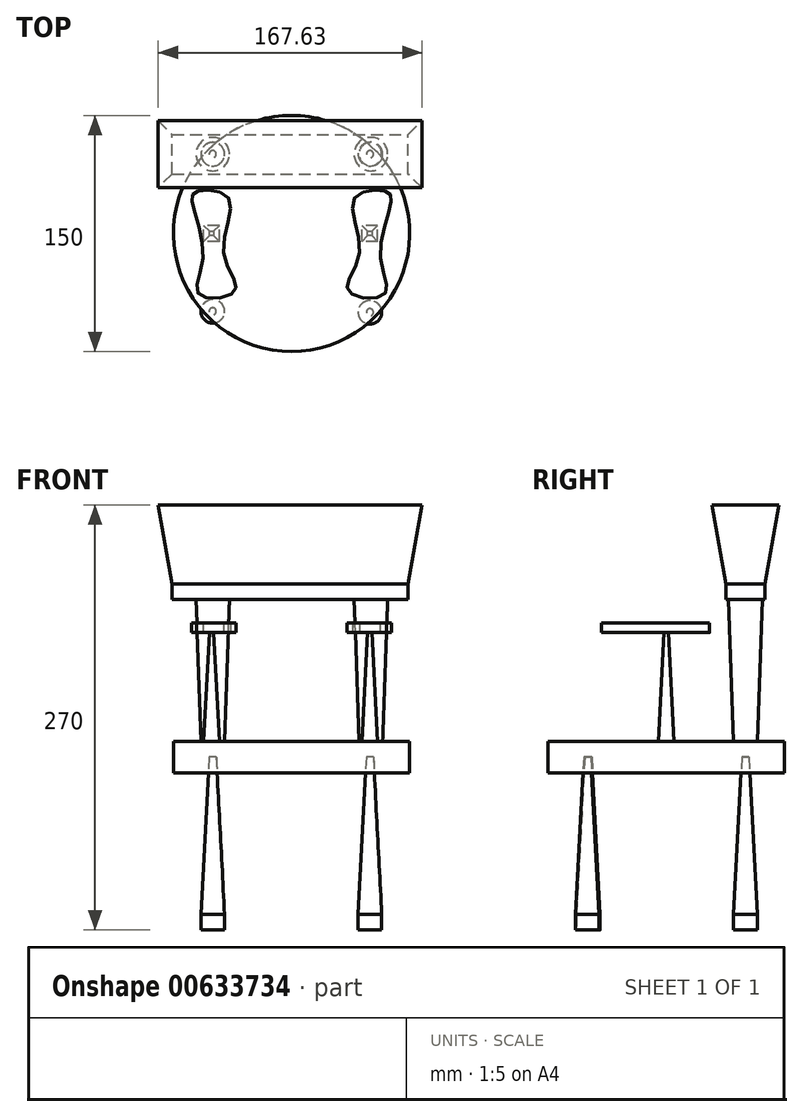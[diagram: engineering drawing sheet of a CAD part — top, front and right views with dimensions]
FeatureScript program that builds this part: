
annotation { "Feature Type Name" : "Feature", "Feature Type Description" : "" }
export const myFeature = defineFeature(function(context is Context, id is Id, definition is map)
    precondition{}
    {
        {
            var Q0;
            Q0=qCreatedBy(makeId("Top.planeOp"),FACE);
            var sketch = newSketch(context, id + "F0", { "sketchPlane" : qUnion([Q0])});
            skCircle(sketch, "E0", {"center": v(-50.07, 50.38) * mm, "radius": 7.5 * mm});
            skCircle(sketch, "E1", {"center": v(49.76, 50.38) * mm, "radius": 7.5 * mm});
            skCircle(sketch, "E2", {"center": v(-50.07, -49.45) * mm, "radius": 7.5 * mm});
            skCircle(sketch, "E3", {"center": v(49.76, -50.07) * mm, "radius": 7.5 * mm});
            skSolve(sketch);
        }
        {
            var Q0;
            Q0=makeQuery(id+"F0.imprint","IMPRINT",FACE,{"disambiguationData":[TD([[makeQuery(id+"F0.imprint","IMPRINT",EDGE,{"derivedFrom":sQuery(id+"F0.wireOp",EDGE,"E1")}),1.0]])]});
            var Q1;
            Q1=makeQuery(id+"F0.imprint","IMPRINT",FACE,{"disambiguationData":[TD([[makeQuery(id+"F0.imprint","IMPRINT",EDGE,{"derivedFrom":sQuery(id+"F0.wireOp",EDGE,"E0")}),1.0]])]});
            var Q2;
            Q2=makeQuery(id+"F0.imprint","IMPRINT",FACE,{"disambiguationData":[TD([[makeQuery(id+"F0.imprint","IMPRINT",EDGE,{"derivedFrom":sQuery(id+"F0.wireOp",EDGE,"E2")}),1.0]])]});
            var Q3;
            Q3=makeQuery(id+"F0.imprint","IMPRINT",FACE,{"disambiguationData":[TD([[makeQuery(id+"F0.imprint","IMPRINT",EDGE,{"derivedFrom":sQuery(id+"F0.wireOp",EDGE,"E3")}),1.0]])]});
            extrude(context, id + "F1", {"entities" : qUnion([Q0, Q1, Q2, Q3]), "depth" : 100 * mm, "offsetDistance" : 25 * mm, "hasDraft" : true, "draftAngle" : 3 * degree, "draftPullDirection" : true, "hasSecondDirection" : true, "secondDirectionOppositeDirection" : true, "secondDirectionDepth" : 10 * mm});
        }
        {
            var Q0;
            Q0=qCreatedBy(makeId("Top.planeOp"),FACE);
            cPlane(context, id + "F2", {"entities" : qUnion([Q0]), "cplaneType" : CPlaneType.OFFSET, "offset" : 100 * mm, "width" : 150 * mm, "height" : 150 * mm});
        }
        {
            var Q0;
            Q0=qCreatedBy(id+"F2.planeOp",FACE);
            var sketch = newSketch(context, id + "F3", { "sketchPlane" : qUnion([Q0])});
            skCircle(sketch, "E4", {"center": v(0, 0) * mm, "radius": 75 * mm});
            skSolve(sketch);
        }
        {
            var Q0;
            Q0=makeQuery(id+"F3.imprint","IMPRINT",FACE,{"disambiguationData":[TD([[makeQuery(id+"F3.imprint","IMPRINT",EDGE,{"derivedFrom":sQuery(id+"F3.wireOp",EDGE,"E4")}),1.0]])]});
            extrude(context, id + "F4", {"entities" : qUnion([Q0]), "depth" : 10 * mm, "offsetDistance" : 25 * mm, "hasSecondDirection" : true, "secondDirectionOppositeDirection" : true, "secondDirectionDepth" : 10 * mm});
        }
        {
            var Q0;
            Q0=qCreatedBy(id+"F2.planeOp",FACE);
            cPlane(context, id + "F5", {"entities" : qUnion([Q0]), "cplaneType" : CPlaneType.OFFSET, "offset" : 10 * mm, "width" : 150 * mm, "height" : 150 * mm});
        }
        {
            var Q0;
            Q0=qCreatedBy(id+"F5.planeOp",FACE);
            var sketch = newSketch(context, id + "F6", { "sketchPlane" : qUnion([Q0])});
            skCircle(sketch, "E5", {"center": v(-50.07, 50.38) * mm, "radius": 7.5 * mm});
            skCircle(sketch, "E6", {"center": v(50.38, 50.38) * mm, "radius": 7.5 * mm});
            skSolve(sketch);
        }
        {
            var Q0;
            Q0 = qSketchRegion(id + "F6", true);
            extrude(context, id + "F7", {"entities" : qUnion([Q0]), "operationType" : NewBodyOperationType.ADD, "depth" : 100 * mm, "offsetDistance" : 25 * mm, "hasDraft" : true, "draftAngle" : 2 * degree});
        }
        {
            var Q0;
            Q0=qCreatedBy(id+"F5.planeOp",FACE);
            cPlane(context, id + "F8", {"entities" : qUnion([Q0]), "cplaneType" : CPlaneType.OFFSET, "offset" : 100 * mm, "width" : 150 * mm, "height" : 150 * mm});
        }
        {
            var Q0;
            Q0=qCreatedBy(id+"F8.planeOp",FACE);
            var sketch = newSketch(context, id + "F9", { "sketchPlane" : qUnion([Q0])});
            skLineSegment(sketch, "E7.bottom", {"start": v(-75.93, 37.83) * mm, "end": v(74.07, 37.83) * mm});
            skLineSegment(sketch, "E7.top", {"start": v(-75.93, 62.83) * mm, "end": v(74.07, 62.83) * mm});
            skLineSegment(sketch, "E7.left", {"start": v(-75.93, 37.83) * mm, "end": v(-75.93, 62.83) * mm});
            skLineSegment(sketch, "E7.right", {"start": v(74.07, 37.83) * mm, "end": v(74.07, 62.83) * mm});
            skSolve(sketch);
        }
        {
            var Q0;
            Q0 = qSketchRegion(id + "F9", true);
            extrude(context, id + "F10", {"entities" : qUnion([Q0]), "operationType" : NewBodyOperationType.ADD, "depth" : 50 * mm, "offsetDistance" : 25 * mm, "hasDraft" : true, "draftAngle" : 10 * degree, "hasSecondDirection" : true, "secondDirectionOppositeDirection" : true, "secondDirectionDepth" : 10 * mm});
        }
        {
            var Q0;
            Q0=qCreatedBy(id+"F5.planeOp",FACE);
            var sketch = newSketch(context, id + "F11", { "sketchPlane" : qUnion([Q0])});
            skLineSegment(sketch, "E8.bottom", {"start": v(-45.8, -5) * mm, "end": v(-55.8, -5) * mm});
            skLineSegment(sketch, "E8.top", {"start": v(-45.8, 5) * mm, "end": v(-55.8, 5) * mm});
            skLineSegment(sketch, "E8.left", {"start": v(-45.8, -5) * mm, "end": v(-45.8, 5) * mm});
            skLineSegment(sketch, "E8.right", {"start": v(-55.8, -5) * mm, "end": v(-55.8, 5) * mm});
            skPoint(sketch, "E8.middle", {"position": v(-50.8, 0) * mm});
            skLineSegment(sketch, "E9.bottom", {"start": v(54.63, -5) * mm, "end": v(44.63, -5) * mm});
            skLineSegment(sketch, "E9.top", {"start": v(54.63, 5) * mm, "end": v(44.63, 5) * mm});
            skLineSegment(sketch, "E9.left", {"start": v(54.63, -5) * mm, "end": v(54.63, 5) * mm});
            skLineSegment(sketch, "E9.right", {"start": v(44.63, -5) * mm, "end": v(44.63, 5) * mm});
            skPoint(sketch, "E9.middle", {"position": v(49.63, 0) * mm});
            skSolve(sketch);
        }
        {
            var Q0;
            Q0 = qSketchRegion(id + "F11", true);
            extrude(context, id + "F12", {"entities" : qUnion([Q0]), "operationType" : NewBodyOperationType.ADD, "depth" : 70 * mm, "offsetDistance" : 25 * mm, "hasDraft" : true, "draftAngle" : 3 * degree, "draftPullDirection" : true, "hasSecondDirection" : true, "secondDirectionOppositeDirection" : true, "secondDirectionDepth" : 10 * mm});
        }
        {
            var Q0;
            Q0=qCreatedBy(id+"F5.planeOp",FACE);
            cPlane(context, id + "F13", {"entities" : qUnion([Q0]), "cplaneType" : CPlaneType.OFFSET, "offset" : 70 * mm, "width" : 150 * mm, "height" : 150 * mm});
        }
        {
            var Q0;
            Q0=qCreatedBy(id+"F13.planeOp",FACE);
            var sketch = newSketch(context, id + "F14", { "sketchPlane" : qUnion([Q0])});
            skFitSpline(sketch, "E10", {"points": [v(-59.43, 26.92) * mm, v(-39.82, 22.2) * mm, v(-42.96, -13.1) * mm, v(-35.9, -36.64) * mm, v(-58.65, -38.99) * mm, v(-56.3, -14.67) * mm, v(-63.36, 21.42) * mm, v(-59.43, 26.92) * mm]});
            skSolve(sketch);
        }
        {
            var Q0;
            Q0=makeQuery(id+"F14.imprint","IMPRINT",FACE,{"disambiguationData":[TD([[makeQuery(id+"F14.imprint","IMPRINT",EDGE,{"derivedFrom":sQuery(id+"F14.wireOp",EDGE,"E10")}),-1.0]])]});
            var Q1;
            Q1=sQuery(id+"F14.wireOp",EDGE,"E10");
            extrude(context, id + "F15", {"entities" : qUnion([Q0]), "surfaceEntities" : qUnion([Q1]), "depth" : 5 * mm, "offsetDistance" : 25 * mm, "hasSecondDirection" : true, "secondDirectionOppositeDirection" : true, "secondDirectionDepth" : 1 * mm});
        }
        {
            var Q0;
            Q0=makeQuery(id+"F15.opExtrude","SWEPT_BODY",BODY,{"disambiguationData":[OSD([sQuery(id+"F14.wireOp",EDGE,"E10")])]});
            var Q1;
            Q1=qCreatedBy(makeId("Right.planeOp"),FACE);
            mirror(context, id + "F16", {"operationType" : NewBodyOperationType.ADD, "entities" : qUnion([Q0]), "mirrorPlane" : qUnion([Q1])});
        }
    });
